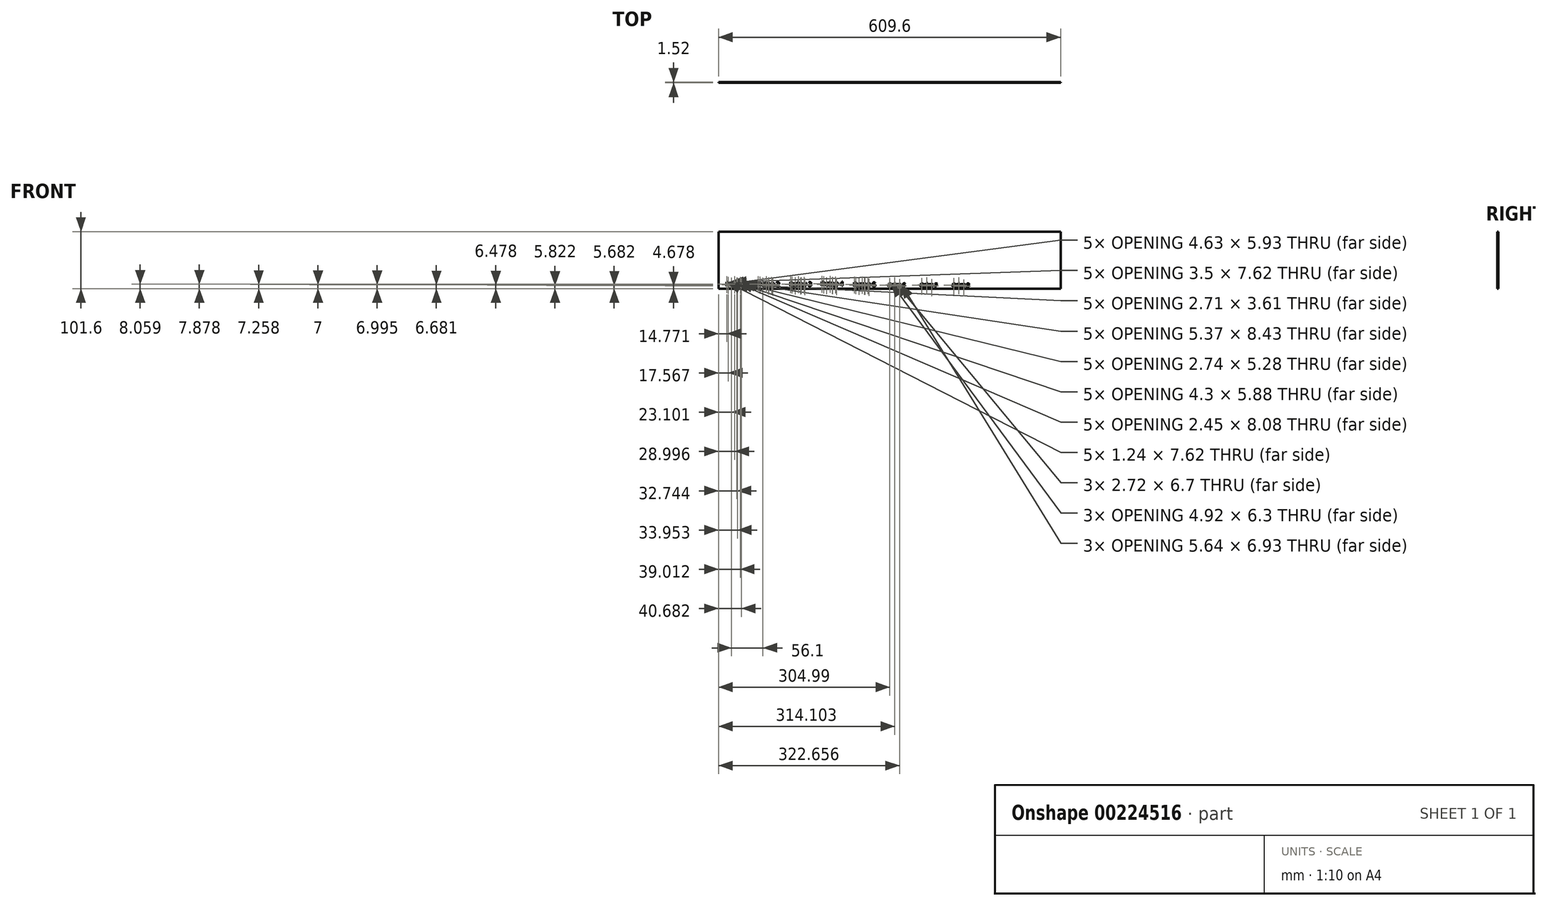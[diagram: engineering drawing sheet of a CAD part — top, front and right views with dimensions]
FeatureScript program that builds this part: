
annotation { "Feature Type Name" : "Feature", "Feature Type Description" : "" }
export const myFeature = defineFeature(function(context is Context, id is Id, definition is map)
    precondition{}
    {
        {
            var Q0;
            Q0=qCreatedBy(makeId("Front.planeOp"),FACE);
            var sketch = newSketch(context, id + "F0", { "sketchPlane" : qUnion([Q0])});
            skLineSegment(sketch, "E0.bottom", {"start": v(0, 0) * mm, "end": v(609.6, 0) * mm});
            skLineSegment(sketch, "E0.top", {"start": v(0, 101.6) * mm, "end": v(609.6, 101.6) * mm});
            skLineSegment(sketch, "E0.left", {"start": v(0, 0) * mm, "end": v(0, 101.6) * mm});
            skLineSegment(sketch, "E0.right", {"start": v(609.6, 0) * mm, "end": v(609.6, 101.6) * mm});
            skSolve(sketch);
        }
        {
            var Q0;
            Q0=makeQuery(id+"F0.imprint","IMPRINT",FACE,{"disambiguationData":[TD([[makeQuery(id+"F0.imprint","IMPRINT",EDGE,{"derivedFrom":sQuery(id+"F0.wireOp",EDGE,"E0.bottom")}),1.0]])]});
            extrude(context, id + "F1", {"entities" : qUnion([Q0]), "oppositeDirection" : true, "depth" : 1.52 * mm});
        }
        {
            var Q0;
            Q0=makeQuery(id+"F1.opExtrude","CAP_FACE",FACE,{"disambiguationData":[OSD([sQuery(id+"F0.wireOp",EDGE,"E0.bottom"),sQuery(id+"F0.wireOp",EDGE,"E0.top"),sQuery(id+"F0.wireOp",EDGE,"E0.left"),sQuery(id+"F0.wireOp",EDGE,"E0.right")])],"isStart":true});
            var sketch = newSketch(context, id + "F2", { "sketchPlane" : qUnion([Q0])});
            skText(sketch, "E1", { "text": "Relay 1", "fontName": "AllertaStencil-Regular.ttf"});
            skText(sketch, "E2", { "text": "Relay 2", "fontName": "AllertaStencil-Regular.ttf"});
            skText(sketch, "E3", { "text": "Relay 3", "fontName": "AllertaStencil-Regular.ttf"});
            skText(sketch, "E4", { "text": "Relay 4", "fontName": "AllertaStencil-Regular.ttf"});
            skText(sketch, "E5", { "text": "Relay 5", "fontName": "AllertaStencil-Regular.ttf"});
            skText(sketch, "E6", { "text": "Relay 6", "fontName": "OpenSans-BoldItalic.ttf"});
            skText(sketch, "E7", { "text": "Relay 7", "fontName": "OpenSans-BoldItalic.ttf"});
            skText(sketch, "E8", { "text": "Relay 8", "fontName": "OpenSans-BoldItalic.ttf"});
            skLineSegment(sketch, "E9", {"start": v(31.75, 101.6) * mm, "end": v(31.75, 0) * mm, "construction": true});
            skLineSegment(sketch, "E10", {"start": v(88.9, 101.6) * mm, "end": v(88.9, 0) * mm});
            skLineSegment(sketch, "E11", {"start": v(146.05, 101.6) * mm, "end": v(146.05, 0) * mm});
            skLineSegment(sketch, "E12", {"start": v(203.2, 101.6) * mm, "end": v(203.2, 0) * mm});
            skLineSegment(sketch, "E13", {"start": v(260.35, 101.6) * mm, "end": v(260.35, 0) * mm});
            skLineSegment(sketch, "E14", {"start": v(317.5, 101.6) * mm, "end": v(317.5, 0) * mm});
            skLineSegment(sketch, "E15", {"start": v(374.65, 101.5) * mm, "end": v(374.65, 0) * mm});
            skLineSegment(sketch, "E16", {"start": v(431.8, 102.05) * mm, "end": v(431.8, 3.5) * mm});
            const initialGuessF2  = {"E1": [0.01322, 0.00407, 1, 0, 0.00762], "E2": [0.06932, 0.00418, 1, 0, 0.00762], "E3": [0.12666, 0.00432, 1, 0, 0.00762], "E4": [0.183, 0.0048, 1, 0, 0.00762], "E5": [0.24064, 0.0035, 1, 0, 0.00762], "E6": [0.3023, 0.00333, 1, 0, 0.00635], "E7": [0.35956, 0.0033, 1, 0, 0.00635], "E8": [0.4165, 0.00317, 1, 0, 0.00635]};
            skSetInitialGuess(sketch, initialGuessF2);
            skSolve(sketch);
        }
        {
            var Q0;
            Q0 = qSketchRegion(id + "F2", true);
            extrude(context, id + "F3", {"entities" : qUnion([Q0]), "operationType" : NewBodyOperationType.REMOVE, "endBound" : BoundingType.THROUGH_ALL, "oppositeDirection" : true, "depth" : 25.4 * mm});
        }
    });
